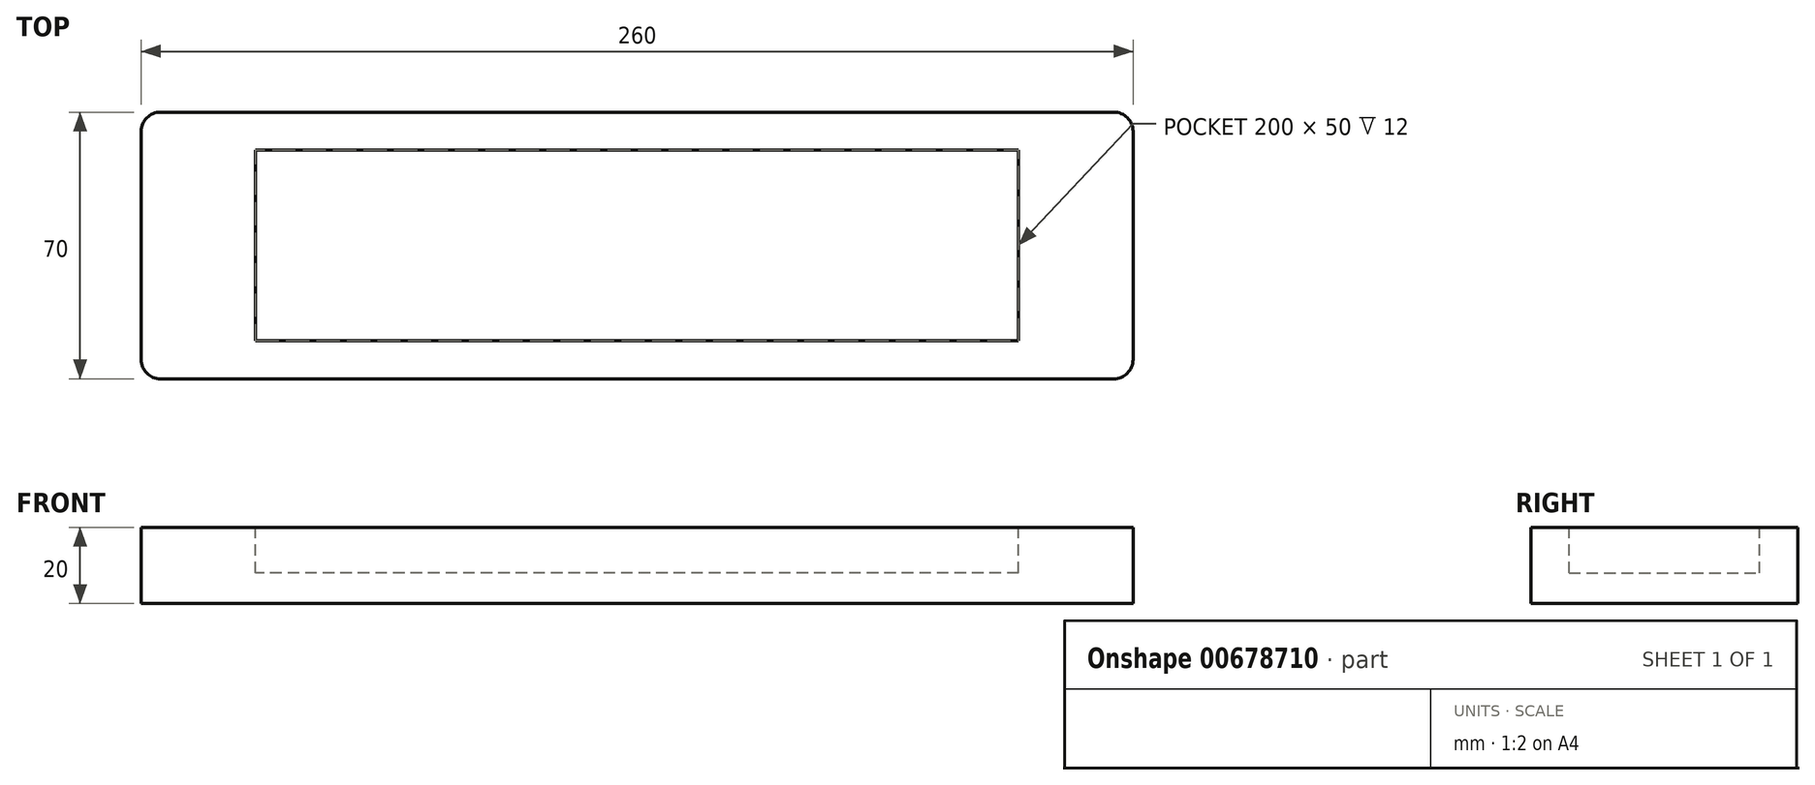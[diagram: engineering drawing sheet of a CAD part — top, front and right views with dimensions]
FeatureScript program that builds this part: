
annotation { "Feature Type Name" : "Feature", "Feature Type Description" : "" }
export const myFeature = defineFeature(function(context is Context, id is Id, definition is map)
    precondition{}
    {
        {
            var Q0;
            Q0=qCreatedBy(makeId("Top.planeOp"),FACE);
            var sketch = newSketch(context, id + "F0", { "sketchPlane" : qUnion([Q0])});
            skLineSegment(sketch, "E0.bottom", {"start": v(130, -35) * mm, "end": v(-130, -35) * mm});
            skLineSegment(sketch, "E0.top", {"start": v(130, 35) * mm, "end": v(-130, 35) * mm});
            skLineSegment(sketch, "E0.left", {"start": v(130, -35) * mm, "end": v(130, 35) * mm});
            skLineSegment(sketch, "E0.right", {"start": v(-130, -35) * mm, "end": v(-130, 35) * mm});
            skPoint(sketch, "E0.middle", {"position": v(0, 0) * mm});
            skSolve(sketch);
        }
        {
            var Q0;
            Q0=makeQuery(id+"F0.imprint","IMPRINT",FACE,{"disambiguationData":[TD([[makeQuery(id+"F0.imprint","IMPRINT",EDGE,{"derivedFrom":sQuery(id+"F0.wireOp",EDGE,"E0.bottom")}),-1.0]])]});
            extrude(context, id + "F1", {"entities" : qUnion([Q0]), "depth" : 20 * mm, "offsetDistance" : 25 * mm});
        }
        {
            var Q0;
            Q0=makeQuery(id+"F1.opExtrude","CAP_FACE",FACE,{"disambiguationData":[OSD([sQuery(id+"F0.wireOp",EDGE,"E0.bottom"),sQuery(id+"F0.wireOp",EDGE,"E0.top"),sQuery(id+"F0.wireOp",EDGE,"E0.left"),sQuery(id+"F0.wireOp",EDGE,"E0.right")])],"isStart":false});
            var sketch = newSketch(context, id + "F2", { "sketchPlane" : qUnion([Q0])});
            skLineSegment(sketch, "E1.bottom", {"start": v(100, -25) * mm, "end": v(-100, -25) * mm});
            skLineSegment(sketch, "E1.top", {"start": v(100, 25) * mm, "end": v(-100, 25) * mm});
            skLineSegment(sketch, "E1.left", {"start": v(100, -25) * mm, "end": v(100, 25) * mm});
            skLineSegment(sketch, "E1.right", {"start": v(-100, -25) * mm, "end": v(-100, 25) * mm});
            skPoint(sketch, "E1.middle", {"position": v(0, 0) * mm});
            skSolve(sketch);
        }
        {
            var Q0;
            Q0=makeQuery(id+"F2.imprint","IMPRINT",FACE,{"disambiguationData":[TD([[makeQuery(id+"F2.imprint","IMPRINT",EDGE,{"derivedFrom":sQuery(id+"F2.wireOp",EDGE,"E1.bottom")}),-1.0]])]});
            extrude(context, id + "F3", {"entities" : qUnion([Q0]), "operationType" : NewBodyOperationType.REMOVE, "oppositeDirection" : true, "depth" : 12 * mm, "offsetDistance" : 25 * mm});
        }
        {
            var Q0;
            Q0=makeQuery(id+"F1.opExtrude","SWEPT_EDGE",EDGE,{"disambiguationData":[OSD([sQuery(id+"F0.wireOp",EDGE,"E0.bottom"),sQuery(id+"F0.wireOp",EDGE,"E0.right")])]});
            var Q1;
            Q1=makeQuery(id+"F1.opExtrude","SWEPT_EDGE",EDGE,{"disambiguationData":[OSD([sQuery(id+"F0.wireOp",EDGE,"E0.bottom"),sQuery(id+"F0.wireOp",EDGE,"E0.left")])]});
            var Q2;
            Q2=makeQuery(id+"F1.opExtrude","SWEPT_EDGE",EDGE,{"disambiguationData":[OSD([sQuery(id+"F0.wireOp",EDGE,"E0.top"),sQuery(id+"F0.wireOp",EDGE,"E0.left")])]});
            var Q3;
            Q3=makeQuery(id+"F1.opExtrude","SWEPT_EDGE",EDGE,{"disambiguationData":[OSD([sQuery(id+"F0.wireOp",EDGE,"E0.top"),sQuery(id+"F0.wireOp",EDGE,"E0.right")])]});
            fillet(context, id + "F4", {"entities" : qUnion([Q0, Q1, Q2, Q3]), "radius" : 5 * mm, "tangentPropagation" : true, "allowEdgeOverflow" : false});
        }
    });
